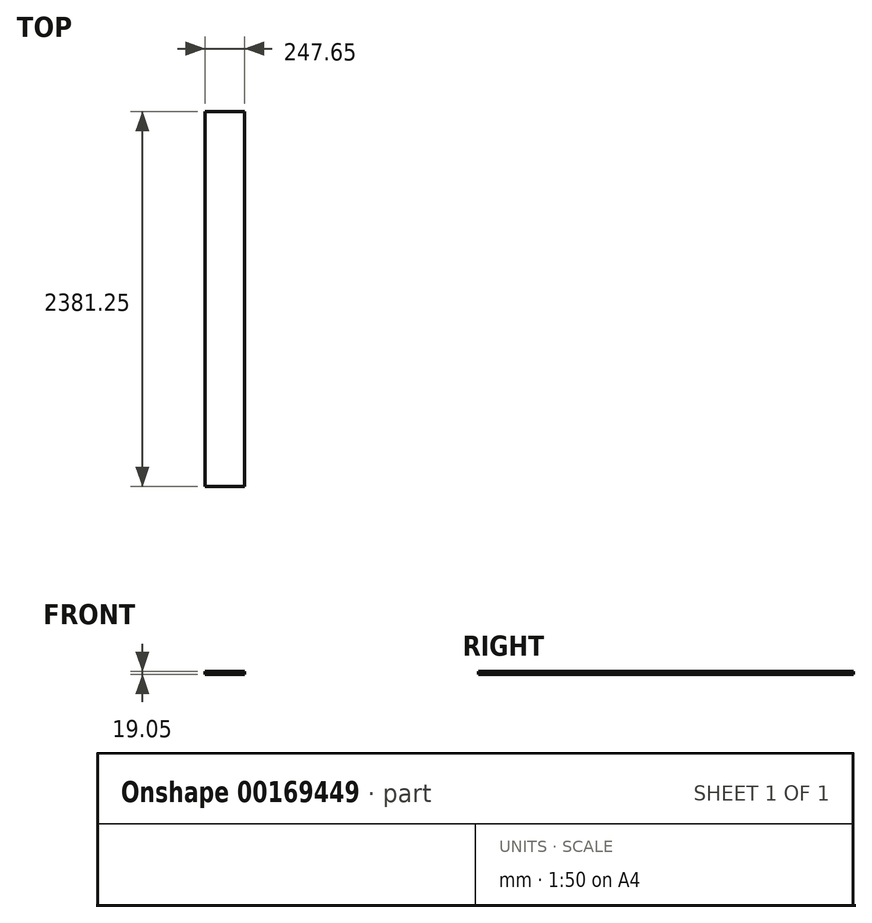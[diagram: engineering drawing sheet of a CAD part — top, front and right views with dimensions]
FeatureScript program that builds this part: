
annotation { "Feature Type Name" : "Feature", "Feature Type Description" : "" }
export const myFeature = defineFeature(function(context is Context, id is Id, definition is map)
    precondition{}
    {
        {
            var Q0;
            Q0=qCreatedBy(makeId("Top.planeOp"),FACE);
            var sketch = newSketch(context, id + "F0", { "sketchPlane" : qUnion([Q0])});
            skPoint(sketch, "E0.orphan", {"position": v(0, -523) * mm});
            skLineSegment(sketch, "E1.bottom", {"start": v(0, 1406.51) * mm, "end": v(247.65, 1406.51) * mm});
            skLineSegment(sketch, "E1.top", {"start": v(0, -974.74) * mm, "end": v(247.65, -974.74) * mm});
            skLineSegment(sketch, "E1.left", {"start": v(0, 1406.51) * mm, "end": v(0, -974.74) * mm});
            skLineSegment(sketch, "E1.right", {"start": v(247.65, 1406.51) * mm, "end": v(247.65, -974.74) * mm});
            skSolve(sketch);
        }
        {
            var Q0;
            Q0 = qSketchRegion(id + "F0", true);
            extrude(context, id + "F1", {"entities" : qUnion([Q0]), "depth" : 19.05 * mm});
        }
    });
